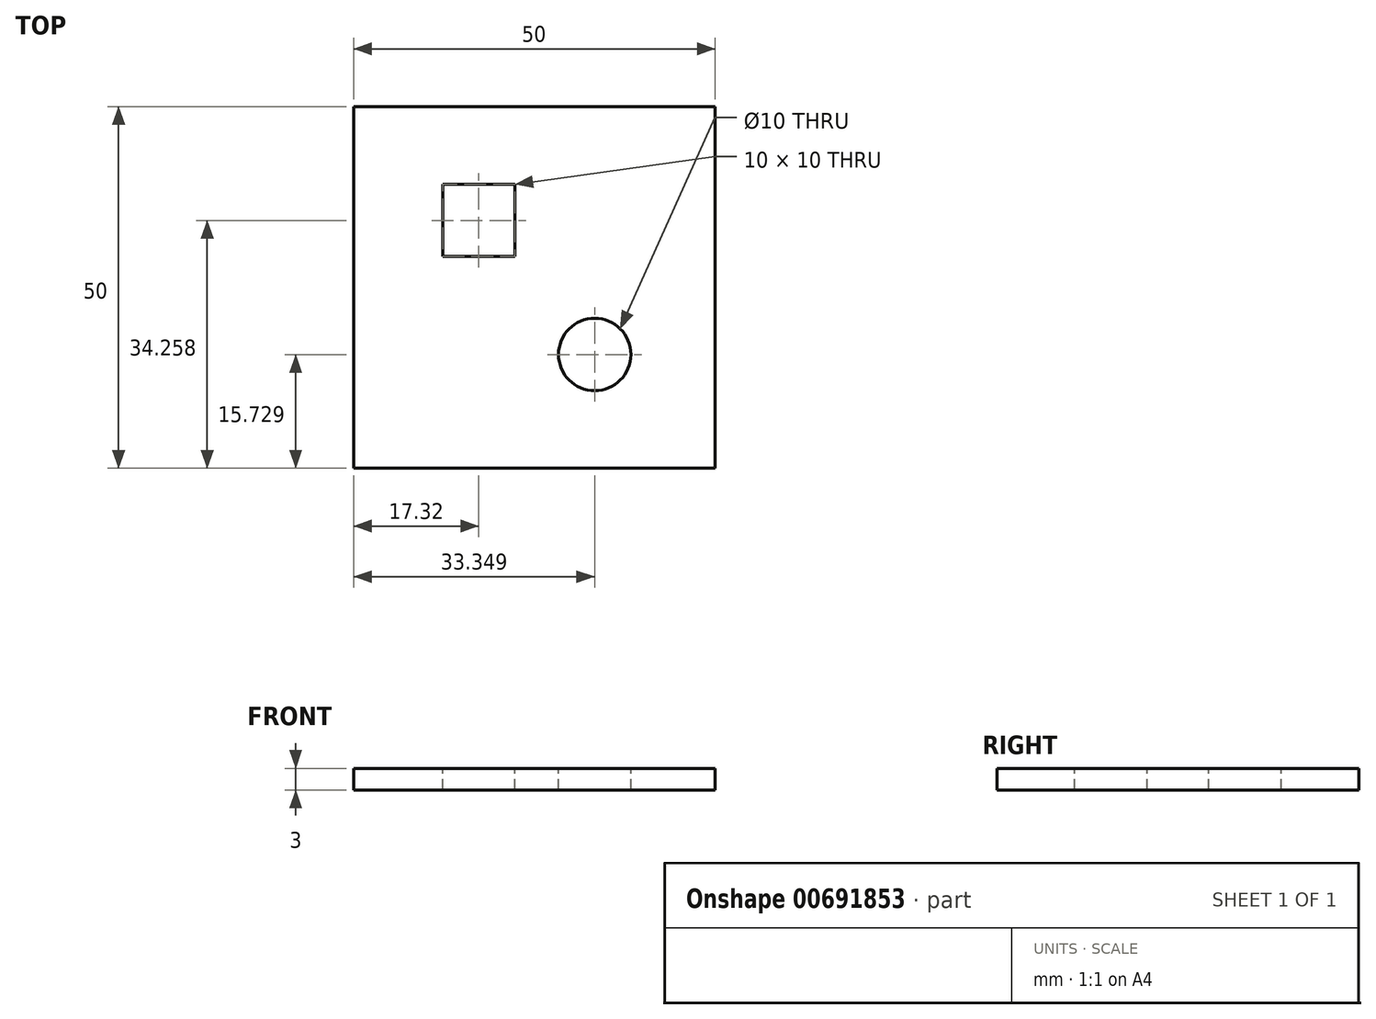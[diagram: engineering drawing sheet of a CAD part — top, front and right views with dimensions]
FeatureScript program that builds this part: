
annotation { "Feature Type Name" : "Feature", "Feature Type Description" : "" }
export const myFeature = defineFeature(function(context is Context, id is Id, definition is map)
    precondition{}
    {
        {
            var Q0;
            Q0=qCreatedBy(makeId("Top.planeOp"),FACE);
            var sketch = newSketch(context, id + "F0", { "sketchPlane" : qUnion([Q0])});
            skLineSegment(sketch, "E0.bottom", {"start": v(-25, -25) * mm, "end": v(25, -25) * mm});
            skLineSegment(sketch, "E0.top", {"start": v(-25, 25) * mm, "end": v(25, 25) * mm});
            skLineSegment(sketch, "E0.left", {"start": v(-25, -25) * mm, "end": v(-25, 25) * mm});
            skLineSegment(sketch, "E0.right", {"start": v(25, -25) * mm, "end": v(25, 25) * mm});
            skSolve(sketch);
        }
        {
            var Q0;
            Q0=makeQuery(id+"F0.imprint","IMPRINT",FACE,{"disambiguationData":[TD([[makeQuery(id+"F0.imprint","IMPRINT",EDGE,{"derivedFrom":sQuery(id+"F0.wireOp",EDGE,"E0.bottom")}),1.0]])]});
            extrude(context, id + "F1", {"entities" : qUnion([Q0]), "depth" : 3 * mm, "offsetDistance" : 25 * mm});
        }
        {
            var Q0;
            Q0=makeQuery(id+"F1.opExtrude","CAP_FACE",FACE,{"disambiguationData":[OSD([sQuery(id+"F0.wireOp",EDGE,"E0.bottom"),sQuery(id+"F0.wireOp",EDGE,"E0.top"),sQuery(id+"F0.wireOp",EDGE,"E0.left"),sQuery(id+"F0.wireOp",EDGE,"E0.right")])],"isStart":false});
            var sketch = newSketch(context, id + "F2", { "sketchPlane" : qUnion([Q0])});
            skLineSegment(sketch, "E1.bottom", {"start": v(-12.68, 14.26) * mm, "end": v(-2.68, 14.26) * mm});
            skLineSegment(sketch, "E1.top", {"start": v(-12.68, 4.26) * mm, "end": v(-2.68, 4.26) * mm});
            skLineSegment(sketch, "E1.left", {"start": v(-12.68, 14.26) * mm, "end": v(-12.68, 4.26) * mm});
            skLineSegment(sketch, "E1.right", {"start": v(-2.68, 14.26) * mm, "end": v(-2.68, 4.26) * mm});
            skCircle(sketch, "E2", {"center": v(8.35, -9.27) * mm, "radius": 5 * mm});
            skSolve(sketch);
        }
        {
            var Q0;
            Q0=makeQuery(id+"F2.imprint","IMPRINT",FACE,{"disambiguationData":[TD([[makeQuery(id+"F2.imprint","IMPRINT",EDGE,{"derivedFrom":sQuery(id+"F2.wireOp",EDGE,"E1.bottom")}),-1.0]])]});
            var Q1;
            Q1=makeQuery(id+"F2.imprint","IMPRINT",FACE,{"disambiguationData":[TD([[makeQuery(id+"F2.imprint","IMPRINT",EDGE,{"derivedFrom":sQuery(id+"F2.wireOp",EDGE,"E2")}),1.0]])]});
            extrude(context, id + "F3", {"entities" : qUnion([Q0, Q1]), "operationType" : NewBodyOperationType.REMOVE, "oppositeDirection" : true, "depth" : 5 * mm, "offsetDistance" : 25 * mm});
        }
    });
